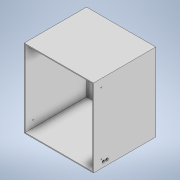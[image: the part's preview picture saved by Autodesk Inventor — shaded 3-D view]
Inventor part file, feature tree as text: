
AUTODESK INVENTOR PART (.ipt)
format: ipt  version: 2020 (Build 240168000, 168)  size: 197,120 bytes
history: native  units: mm
features: extrude x5, sketch x5, shell x1, mirror x1
ambient origin geometry x8: Origin, YZ Plane, XZ Plane, XY Plane, X Axis, Y Axis, Z Axis, Center Point
bodies: Solid1 (feature_tree)
feature tree (12):
  extrude  "Base"  Depth=450.0mm
  shell  "Shell1"  Thickness=360.0mm
  extrude  "Cable Holes"  Depth=5.0mm
  extrude  "Mount Holes inner walls"  Depth=28.75mm
  extrude  "Extrusion5"  Depth=10.0mm
  mirror  "Mirror2"
  extrude  "Fan holes"  Depth=10.0mm
  sketch  "Sketch2"  dims[d0=400.0mm d1=450.0mm d2=360.0mm d3=0.0mm]
  sketch  "Sketch4"  dims[d4=5.0mm d18=15.0mm]
  sketch  "Sketch5"  dims[d19=57.5mm d20=28.75mm]
  sketch  "Sketch6"  dims[d21=20.0mm d23=20.0mm d24=10.0mm d26=10.0mm]
  sketch  "Sketch7"  dims[d28=10.0mm d29=0.0mm d30=309.5mm d31=359.5mm d32=5.5mm d33=20.0mm d35=309.5mm d36=20.0mm d38=359.5mm d41=10.0mm d42=0.0mm d43=5.25mm d44=359.5mm d46=5.25mm d47=340.0mm d48=0.0mm d49=4.3mm d50=20.0mm d52=32.0mm d53=20.0mm d55=32.0mm d58=38.0mm d59=59.0mm d60=45.0deg d61=10.0mm d62=0.0mm d63=309.25mm]
